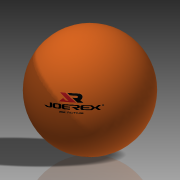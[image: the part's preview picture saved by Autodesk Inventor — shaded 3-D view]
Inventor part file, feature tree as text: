
AUTODESK INVENTOR PART (.ipt)
format: ipt  version: 2013 (Build 170138000, 138)  size: 263,680 bytes
history: native  units: mm
features: other x2, sketch x2, revolve x1, plane x1
ambient origin geometry x8: Origin, YZ Plane, XZ Plane, XY Plane, X Axis, Y Axis, Z Axis, Center Point
bodies: Solid1 (feature_tree)
feature tree (6):
  revolve  "Revolution1"  [1 undecoded]
  plane  "Work Plane2"
  other  "Decal2"
  sketch  "Sketch1"  dims[d0=40.0mm d1=1.0mm]
  sketch  "Sketch5"  dims[d2=90.0deg d6=36.25mm d22=20.0mm d27=7.166667mm d30=10.0mm d31=3.583333mm]
  other  "Image3"
note: 1 required parameter value undecoded (feature->parameter linkage not recoverable at this tier; creation-order binding heuristic only, values carry confidence <= 0.55)
